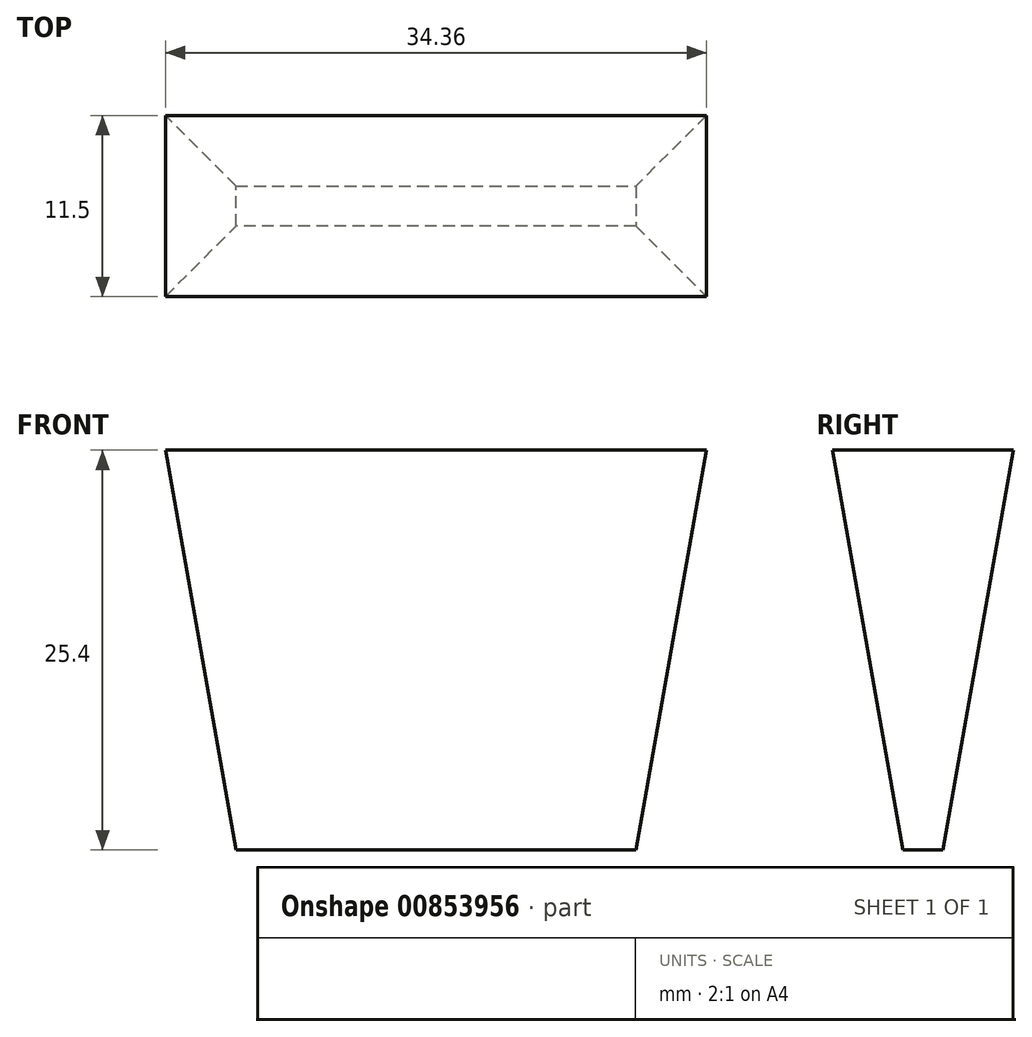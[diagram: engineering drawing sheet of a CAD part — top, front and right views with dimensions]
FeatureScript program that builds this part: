
annotation { "Feature Type Name" : "Feature", "Feature Type Description" : "" }
export const myFeature = defineFeature(function(context is Context, id is Id, definition is map)
    precondition{}
    {
        {
            var Q0;
            Q0=qCreatedBy(makeId("Top.planeOp"),FACE);
            var sketch = newSketch(context, id + "F0", { "sketchPlane" : qUnion([Q0])});
            skPoint(sketch, "E0.middle", {"position": v(0, 0) * mm});
            skLineSegment(sketch, "E1.bottom", {"start": v(12.7, -1.27) * mm, "end": v(-12.7, -1.27) * mm});
            skLineSegment(sketch, "E1.top", {"start": v(12.7, 1.27) * mm, "end": v(-12.7, 1.27) * mm});
            skLineSegment(sketch, "E1.left", {"start": v(12.7, -1.27) * mm, "end": v(12.7, 1.27) * mm});
            skLineSegment(sketch, "E1.right", {"start": v(-12.7, -1.27) * mm, "end": v(-12.7, 1.27) * mm});
            skSolve(sketch);
        }
        {
            var Q0;
            Q0 = qSketchRegion(id + "F0", true);
            extrude(context, id + "F1", {"entities" : qUnion([Q0]), "depth" : 25.4 * mm, "offsetDistance" : 25.4 * mm, "hasDraft" : true, "draftAngle" : 10 * degree});
        }
    });
